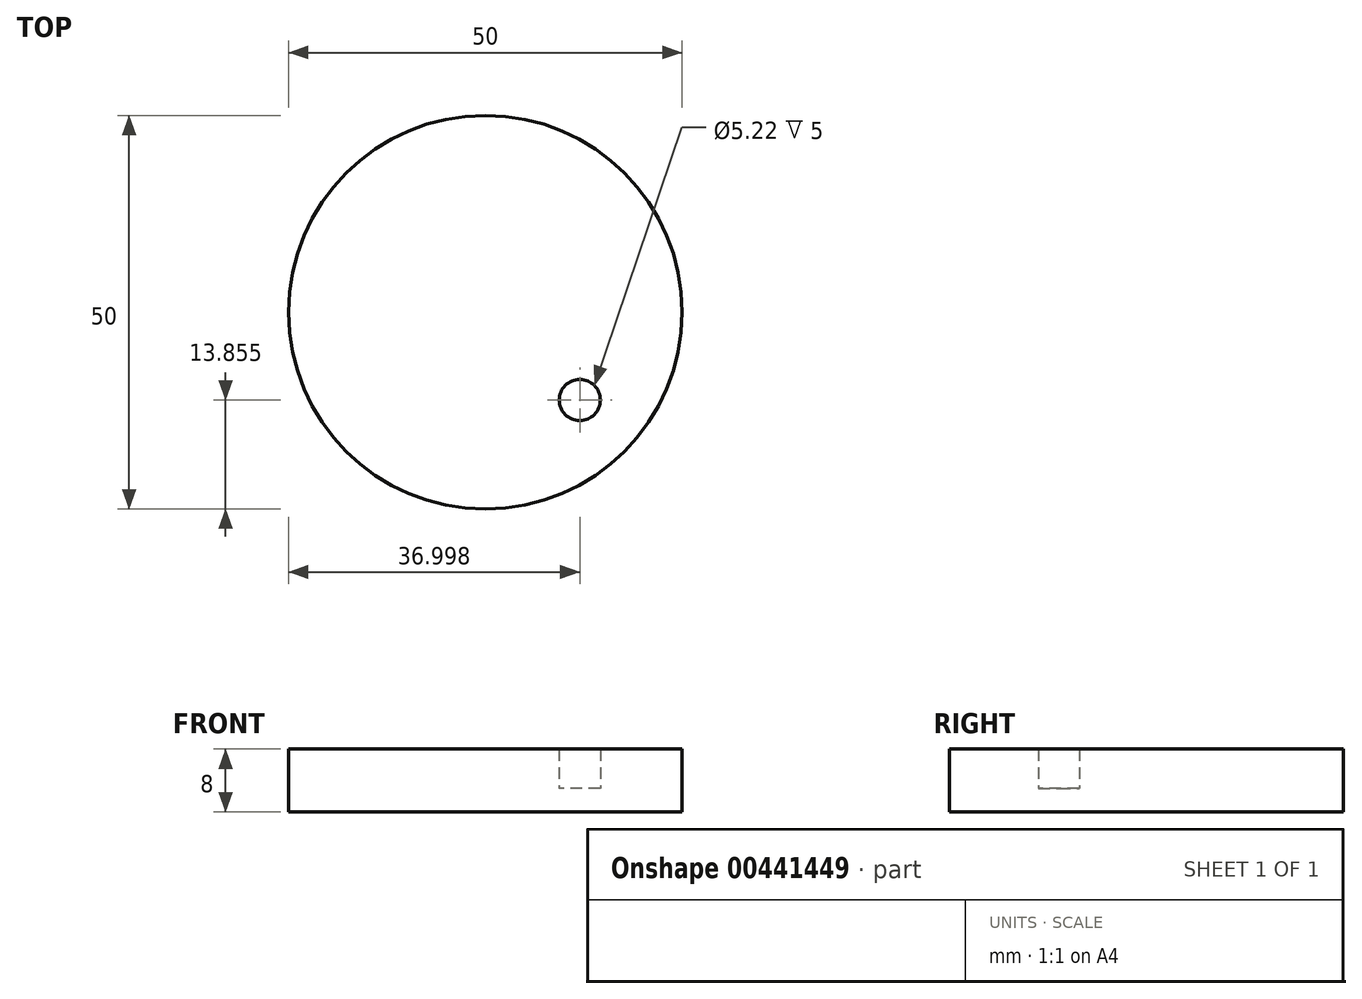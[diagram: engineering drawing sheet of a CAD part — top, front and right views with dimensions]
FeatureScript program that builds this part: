
annotation { "Feature Type Name" : "Feature", "Feature Type Description" : "" }
export const myFeature = defineFeature(function(context is Context, id is Id, definition is map)
    precondition{}
    {
        {
            var Q0;
            Q0=qCreatedBy(makeId("Top.planeOp"),FACE);
            var sketch = newSketch(context, id + "F0", { "sketchPlane" : qUnion([Q0])});
            skCircle(sketch, "E0", {"center": v(0, 0) * mm, "radius": 25 * mm});
            skCircle(sketch, "E1", {"center": v(0, 0) * mm, "radius": 22.5 * mm});
            skCircle(sketch, "E2", {"center": v(-16.47, 7.44) * mm, "radius": 1.5 * mm});
            skCircle(sketch, "E3", {"center": v(-12.18, 12.2) * mm, "radius": 2 * mm});
            skCircle(sketch, "E4", {"center": v(-6.05, 15.87) * mm, "radius": 2.5 * mm});
            skText(sketch, "E5", { "text": "TC", "fontName": "OpenSans-Regular.ttf"});
            skCircle(sketch, "E6", {"center": v(12, -11.15) * mm, "radius": 2.6 * mm});
            skCircle(sketch, "E7", {"center": v(4.06, -16.48) * mm, "radius": 2.6 * mm});
            skLineSegment(sketch, "E8", {"start": v(2.6, -14.31) * mm, "end": v(10.54, -8.98) * mm});
            skLineSegment(sketch, "E9", {"start": v(5.51, -18.64) * mm, "end": v(13.45, -13.3) * mm});
            const initialGuessF0  = {"E5": [-0.00866, -0.00544, 1, 0, 0.01257]};
            skSetInitialGuess(sketch, initialGuessF0);
            skSolve(sketch);
        }
        {
            var Q0;
            Q0=makeQuery(id+"F0.imprint","IMPRINT",FACE,{"disambiguationData":[TD([[makeQuery(id+"F0.imprint","IMPRINT",EDGE,{"derivedFrom":sQuery(id+"F0.wireOp",EDGE,"E1")}),-1.0]])]});
            var Q1;
            Q1=makeQuery(id+"F0.imprint","IMPRINT",FACE,{"disambiguationData":[TD([[makeQuery(id+"F0.imprint","IMPRINT",EDGE,{"derivedFrom":sQuery(id+"F0.wireOp",EDGE,"E2")}),1.0]])]});
            var Q2;
            Q2=makeQuery(id+"F0.imprint","IMPRINT",FACE,{"disambiguationData":[TD([[makeQuery(id+"F0.imprint","IMPRINT",EDGE,{"derivedFrom":sQuery(id+"F0.wireOp",EDGE,"E3")}),1.0]])]});
            var Q3;
            Q3=makeQuery(id+"F0.imprint","IMPRINT",FACE,{"disambiguationData":[TD([[makeQuery(id+"F0.imprint","IMPRINT",EDGE,{"derivedFrom":sQuery(id+"F0.wireOp",EDGE,"E4")}),1.0]])]});
            var Q4;
            {var subQ0=sQuery(id+"F0.wireOp",EDGE,"E8");Q4=makeQuery(id+"F0.imprint","IMPRINT",FACE,{"disambiguationData":[TD([[makeQuery(id+"F0.imprint","IMPRINT",EDGE,{"derivedFrom":subQ0}),-1.0]])]});}
            var Q5;
            {var subQ0=sQuery(id+"F0.wireOp",EDGE,"E7");var subQ1=makeQuery(id+"F0.imprint","INTERSECT",VERTEX,{"derivedFrom":[subQ0,sQuery(id+"F0.wireOp",EDGE,"E8")]});Q5=makeQuery(id+"F0.imprint","IMPRINT",FACE,{"disambiguationData":[TD([[makeQuery(id+"F0.imprint","IMPRINT",EDGE,{"disambiguationData":[TD([[subQ1,-1.0]])],"derivedFrom":subQ0}),1.0]])]});}
            var Q6;
            {var subQ0=sQuery(id+"F0.wireOp",EDGE,"E6");var subQ1=makeQuery(id+"F0.imprint","INTERSECT",VERTEX,{"derivedFrom":[subQ0,sQuery(id+"F0.wireOp",EDGE,"E8")]});Q6=makeQuery(id+"F0.imprint","IMPRINT",FACE,{"disambiguationData":[TD([[makeQuery(id+"F0.imprint","IMPRINT",EDGE,{"disambiguationData":[TD([[subQ1,1.0]])],"derivedFrom":subQ0}),-1.0]])]});}
            var Q7;
            Q7=makeQuery(id+"F0.imprint","IMPRINT",FACE,{"disambiguationData":[TD([[makeQuery(id+"F0.imprint","IMPRINT",EDGE,{"derivedFrom":sQuery(id+"F0.wireOp",EDGE,"E5.sketch_text.stroke-0")}),-1.0]])]});
            var Q8;
            Q8=makeQuery(id+"F0.imprint","IMPRINT",FACE,{"disambiguationData":[TD([[makeQuery(id+"F0.imprint","IMPRINT",EDGE,{"derivedFrom":sQuery(id+"F0.wireOp",EDGE,"E5.sketch_text.stroke-8")}),-1.0]])]});
            extrude(context, id + "F1", {"entities" : qUnion([Q0, Q1, Q2, Q3, Q4, Q5, Q6, Q7, Q8]), "depth" : 5 * mm});
        }
        {
            var Q0;
            Q0=qCreatedBy(makeId("Top.planeOp"),FACE);
            var sketch = newSketch(context, id + "F2", { "sketchPlane" : qUnion([Q0])});
            skCircle(sketch, "E10", {"center": v(0, 0) * mm, "radius": 25 * mm});
            skSolve(sketch);
        }
        {
            var Q0;
            Q0 = qSketchRegion(id + "F2", true);
            extrude(context, id + "F3", {"entities" : qUnion([Q0]), "operationType" : NewBodyOperationType.ADD, "oppositeDirection" : true, "depth" : 3 * mm});
        }
    });
